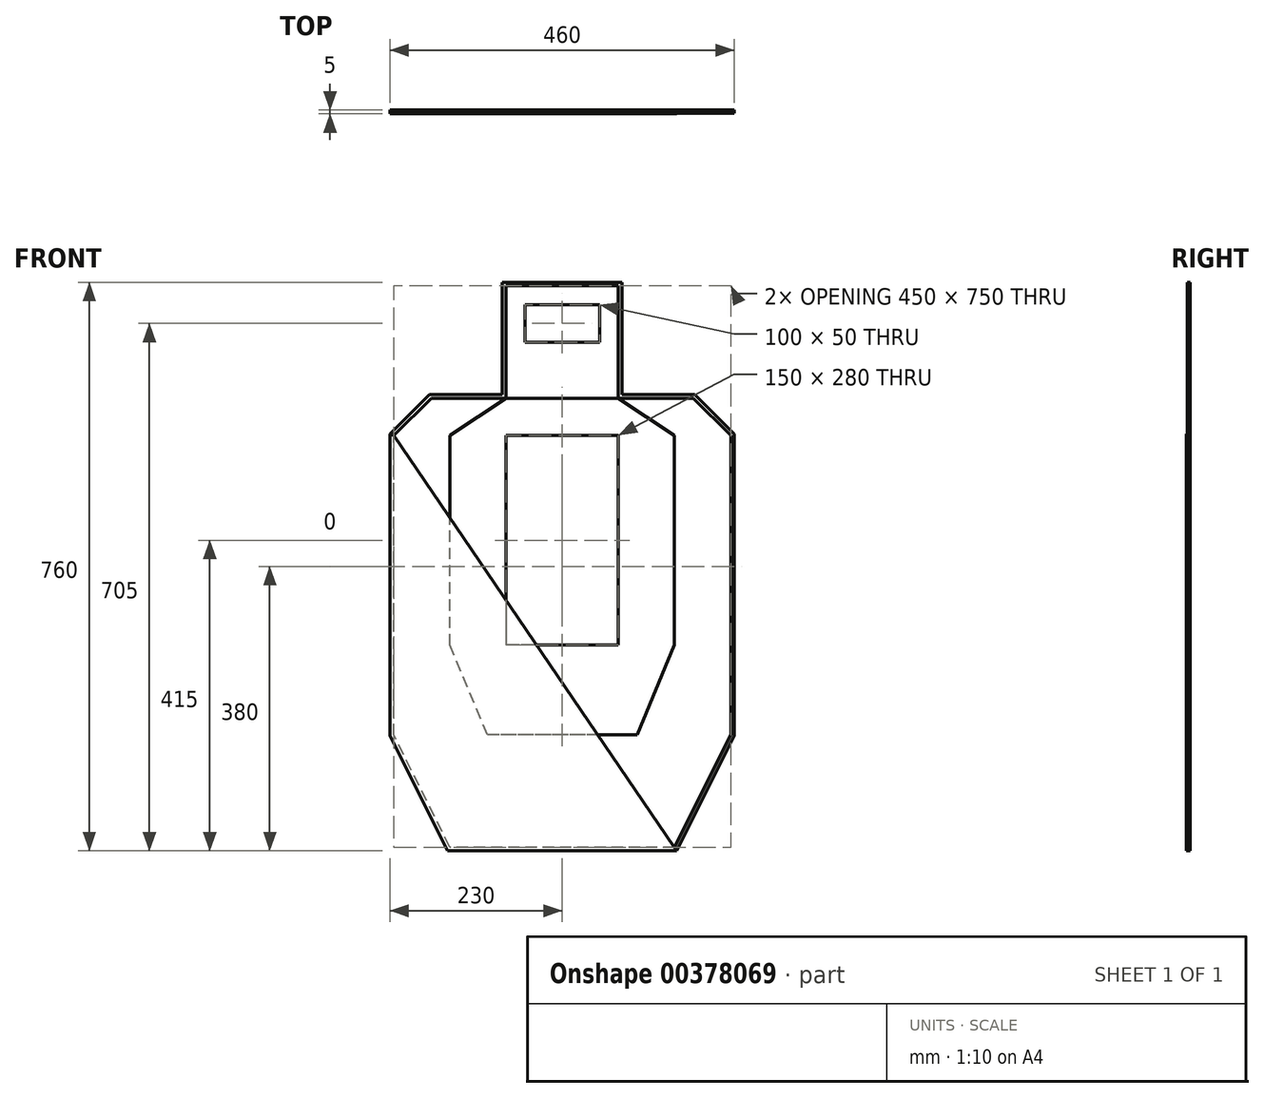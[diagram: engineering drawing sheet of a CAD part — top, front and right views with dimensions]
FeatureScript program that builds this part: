
annotation { "Feature Type Name" : "Feature", "Feature Type Description" : "" }
export const myFeature = defineFeature(function(context is Context, id is Id, definition is map)
    precondition{}
    {
        {
            var Q0;
            Q0=qCreatedBy(makeId("Front.planeOp"),FACE);
            var sketch = newSketch(context, id + "F0", { "sketchPlane" : qUnion([Q0])});
            skLineSegment(sketch, "E0.bottom", {"start": v(0, 100) * mm, "end": v(50, 100) * mm, "construction": true});
            skLineSegment(sketch, "E0.top", {"start": v(0, 125) * mm, "end": v(50, 125) * mm});
            skLineSegment(sketch, "E0.right", {"start": v(50, 100) * mm, "end": v(50, 125) * mm});
            skLineSegment(sketch, "E1.MirrorCS", {"start": v(0, 75) * mm, "end": v(50, 75) * mm});
            skLineSegment(sketch, "E2.MirrorCS", {"start": v(50, 100) * mm, "end": v(50, 75) * mm});
            skLineSegment(sketch, "E3.MirrorCS", {"start": v(0, 0) * mm, "end": v(0, 100) * mm, "construction": true});
            skLineSegment(sketch, "E4.MirrorCS", {"start": v(0, 125) * mm, "end": v(-50, 125) * mm});
            skLineSegment(sketch, "E5.MirrorCS", {"start": v(-50, 100) * mm, "end": v(-50, 125) * mm});
            skLineSegment(sketch, "E6.MirrorCS", {"start": v(-50, 100) * mm, "end": v(-50, 75) * mm});
            skLineSegment(sketch, "E7.MirrorCS", {"start": v(0, 75) * mm, "end": v(-50, 75) * mm});
            skSolve(sketch);
        }
        {
            var Q0;
            Q0=qSketchRegion(id+"F0",true);
            extrude(context, id + "F1", {"entities" : qUnion([Q0]), "oppositeDirection" : true, "depth" : 3 * mm});
        }
        {
            var Q0;
            Q0=qCreatedBy(makeId("Front.planeOp"),FACE);
            var sketch = newSketch(context, id + "F2", { "sketchPlane" : qUnion([Q0])});
            skLineSegment(sketch, "E8", {"start": v(75, 0) * mm, "end": v(75, 150) * mm});
            skLineSegment(sketch, "E9", {"start": v(75, 150) * mm, "end": v(-75, 150) * mm});
            skLineSegment(sketch, "E10", {"start": v(-75, 150) * mm, "end": v(-75, 0) * mm});
            skLineSegment(sketch, "E11", {"start": v(-75, 0) * mm, "end": v(75, 0) * mm});
            skLineSegment(sketch, "E12.0", {"start": v(0, 125) * mm, "end": v(-50, 125) * mm});
            skLineSegment(sketch, "E13.0", {"start": v(0, 125) * mm, "end": v(50, 125) * mm});
            skLineSegment(sketch, "E14.0", {"start": v(50, 100) * mm, "end": v(50, 125) * mm});
            skLineSegment(sketch, "E15.1", {"start": v(50, 100) * mm, "end": v(50, 75) * mm});
            skLineSegment(sketch, "E16.0", {"start": v(0, 75) * mm, "end": v(50, 75) * mm});
            skLineSegment(sketch, "E17.0", {"start": v(0, 75) * mm, "end": v(-50, 75) * mm});
            skLineSegment(sketch, "E18.0", {"start": v(-50, 100) * mm, "end": v(-50, 75) * mm});
            skLineSegment(sketch, "E19.1", {"start": v(-50, 100) * mm, "end": v(-50, 125) * mm});
            skLineSegment(sketch, "E20", {"start": v(0, 125) * mm, "end": v(0, 150) * mm, "construction": true});
            skLineSegment(sketch, "E21", {"start": v(0, 150) * mm, "end": v(0, 137.5) * mm, "construction": true});
            skSolve(sketch);
        }
        {
            var Q0;
            {var subQ0=sQuery(id+"F2.wireOp",EDGE,"E8");Q0=makeQuery(id+"F2.imprint","IMPRINT",FACE,{"disambiguationData":[TD([[makeQuery(id+"F2.imprint","IMPRINT",EDGE,{"derivedFrom":subQ0}),1.0]])]});}
            extrude(context, id + "F3", {"entities" : qUnion([Q0]), "oppositeDirection" : true, "depth" : 3 * mm});
        }
        {
            var Q0;
            Q0=qCreatedBy(makeId("Front.planeOp"),FACE);
            var sketch = newSketch(context, id + "F4", { "sketchPlane" : qUnion([Q0])});
            skLineSegment(sketch, "E22.bottom", {"start": v(75, -50) * mm, "end": v(-75, -50) * mm});
            skLineSegment(sketch, "E22.top", {"start": v(75, -330) * mm, "end": v(-75, -330) * mm});
            skLineSegment(sketch, "E22.left", {"start": v(75, -50) * mm, "end": v(75, -330) * mm});
            skLineSegment(sketch, "E22.right", {"start": v(-75, -50) * mm, "end": v(-75, -330) * mm});
            skLineSegment(sketch, "E23", {"start": v(0, 0) * mm, "end": v(0, -50) * mm, "construction": true});
            skLineSegment(sketch, "E24.0", {"start": v(-75, 0) * mm, "end": v(75, 0) * mm, "construction": true});
            skLineSegment(sketch, "E25", {"start": v(75, 0) * mm, "end": v(75, -50) * mm, "construction": true});
            skSolve(sketch);
        }
        {
            var Q0;
            Q0=makeQuery(id+"F4.imprint","IMPRINT",FACE,{"disambiguationData":[TD([[makeQuery(id+"F4.imprint","IMPRINT",EDGE,{"derivedFrom":sQuery(id+"F4.wireOp",EDGE,"E22.bottom")}),1.0]])]});
            extrude(context, id + "F5", {"entities" : qUnion([Q0]), "oppositeDirection" : true, "depth" : 3 * mm});
        }
        {
            var Q0;
            Q0=qCreatedBy(makeId("Front.planeOp"),FACE);
            var sketch = newSketch(context, id + "F6", { "sketchPlane" : qUnion([Q0])});
            skLineSegment(sketch, "E26.0", {"start": v(-75, 0) * mm, "end": v(75, 0) * mm});
            skLineSegment(sketch, "E27.1", {"start": v(75, -50) * mm, "end": v(75, -330) * mm});
            skLineSegment(sketch, "E28.2", {"start": v(75, -50) * mm, "end": v(-75, -50) * mm});
            skLineSegment(sketch, "E29.3", {"start": v(-75, -50) * mm, "end": v(-75, -330) * mm});
            skLineSegment(sketch, "E30.0", {"start": v(75, -330) * mm, "end": v(-75, -330) * mm});
            skLineSegment(sketch, "E31", {"start": v(75, 0) * mm, "end": v(150, -50) * mm});
            skLineSegment(sketch, "E32", {"start": v(150, -50) * mm, "end": v(150, -330) * mm});
            skLineSegment(sketch, "E33", {"start": v(150, -330) * mm, "end": v(100, -450) * mm});
            skLineSegment(sketch, "E34", {"start": v(100, -450) * mm, "end": v(-100, -450) * mm});
            skLineSegment(sketch, "E35", {"start": v(-100, -450) * mm, "end": v(-150, -330) * mm});
            skLineSegment(sketch, "E36", {"start": v(-150, -330) * mm, "end": v(-150, -50) * mm});
            skLineSegment(sketch, "E37", {"start": v(-150, -50) * mm, "end": v(-75, 0) * mm});
            skLineSegment(sketch, "E38", {"start": v(0, -450) * mm, "end": v(0, -50) * mm, "construction": true});
            skLineSegment(sketch, "E39", {"start": v(150, -50) * mm, "end": v(75, -50) * mm, "construction": true});
            skLineSegment(sketch, "E40", {"start": v(-55.04, -50) * mm, "end": v(-150, -50) * mm, "construction": true});
            skLineSegment(sketch, "E41", {"start": v(150, -330) * mm, "end": v(150, -450) * mm, "construction": true});
            skLineSegment(sketch, "E42", {"start": v(100, -450) * mm, "end": v(150, -450) * mm, "construction": true});
            skLineSegment(sketch, "E43", {"start": v(150, -330) * mm, "end": v(-150, -330) * mm, "construction": true});
            skLineSegment(sketch, "E44", {"start": v(-150, -330) * mm, "end": v(-150, -450) * mm, "construction": true});
            skLineSegment(sketch, "E45", {"start": v(-150, -450) * mm, "end": v(-100, -450) * mm, "construction": true});
            skSolve(sketch);
        }
        {
            var Q0;
            Q0=makeQuery(id+"F6.imprint","IMPRINT",FACE,{"disambiguationData":[TD([[makeQuery(id+"F6.imprint","IMPRINT",EDGE,{"derivedFrom":sQuery(id+"F6.wireOp",EDGE,"E26.0")}),-1.0]])]});
            extrude(context, id + "F7", {"entities" : qUnion([Q0]), "oppositeDirection" : true, "depth" : 3 * mm});
        }
        {
            var Q0;
            Q0=makeQuery(id+"F7.opExtrude","CAP_FACE",FACE,{"disambiguationData":[OSD([sQuery(id+"F6.wireOp",EDGE,"E26.0"),sQuery(id+"F6.wireOp",EDGE,"E27.1"),sQuery(id+"F6.wireOp",EDGE,"E28.2"),sQuery(id+"F6.wireOp",EDGE,"E29.3"),sQuery(id+"F6.wireOp",EDGE,"E30.0"),sQuery(id+"F6.wireOp",EDGE,"E31"),sQuery(id+"F6.wireOp",EDGE,"E32"),sQuery(id+"F6.wireOp",EDGE,"E33"),sQuery(id+"F6.wireOp",EDGE,"E34"),sQuery(id+"F6.wireOp",EDGE,"E35"),sQuery(id+"F6.wireOp",EDGE,"E36"),sQuery(id+"F6.wireOp",EDGE,"E37")])],"isStart":true});
            var sketch = newSketch(context, id + "F8", { "sketchPlane" : qUnion([Q0])});
            skLineSegment(sketch, "E46.0", {"start": v(75, 0) * mm, "end": v(150, -50) * mm});
            skLineSegment(sketch, "E47.0", {"start": v(150, -50) * mm, "end": v(150, -330) * mm});
            skLineSegment(sketch, "E48.0", {"start": v(150, -330) * mm, "end": v(100, -450) * mm});
            skLineSegment(sketch, "E49.1", {"start": v(100, -450) * mm, "end": v(-100, -450) * mm});
            skLineSegment(sketch, "E50.0", {"start": v(-150, -330) * mm, "end": v(-150, -50) * mm});
            skLineSegment(sketch, "E51.0", {"start": v(-100, -450) * mm, "end": v(-150, -330) * mm});
            skLineSegment(sketch, "E52.0", {"start": v(-150, -50) * mm, "end": v(-75, 0) * mm});
            skLineSegment(sketch, "E53", {"start": v(75, 0) * mm, "end": v(175, 0) * mm});
            skLineSegment(sketch, "E54", {"start": v(175, 0) * mm, "end": v(225, -50) * mm});
            skLineSegment(sketch, "E55", {"start": v(225, -50) * mm, "end": v(225, -450) * mm});
            skLineSegment(sketch, "E56", {"start": v(225, -450) * mm, "end": v(150, -600) * mm});
            skLineSegment(sketch, "E57", {"start": v(150, -600) * mm, "end": v(-150, -600) * mm});
            skLineSegment(sketch, "E58", {"start": v(-150, -600) * mm, "end": v(-225, -450) * mm});
            skLineSegment(sketch, "E59", {"start": v(-225, -450) * mm, "end": v(-225, -50) * mm});
            skLineSegment(sketch, "E60", {"start": v(-225, -50) * mm, "end": v(-175, 0) * mm});
            skLineSegment(sketch, "E61", {"start": v(-175, 0) * mm, "end": v(-75, 0) * mm});
            skLineSegment(sketch, "E62", {"start": v(225, -50) * mm, "end": v(225, 0) * mm, "construction": true});
            skLineSegment(sketch, "E63", {"start": v(225, 0) * mm, "end": v(175, 0) * mm, "construction": true});
            skLineSegment(sketch, "E64", {"start": v(225, -450) * mm, "end": v(225, -600) * mm, "construction": true});
            skLineSegment(sketch, "E65", {"start": v(225, -600) * mm, "end": v(150, -600) * mm, "construction": true});
            skLineSegment(sketch, "E66", {"start": v(-225, -450) * mm, "end": v(-225, -600) * mm, "construction": true});
            skLineSegment(sketch, "E67", {"start": v(-225, -600) * mm, "end": v(-150, -600) * mm, "construction": true});
            skLineSegment(sketch, "E68", {"start": v(-175, 0) * mm, "end": v(-225, 0) * mm, "construction": true});
            skLineSegment(sketch, "E69", {"start": v(-225, 0) * mm, "end": v(-225, -50) * mm, "construction": true});
            skSolve(sketch);
        }
        {
            var Q0;
            Q0=qSketchRegion(id+"F8",true);
            extrude(context, id + "F9", {"entities" : qUnion([Q0]), "oppositeDirection" : true, "depth" : 3 * mm});
        }
        {
            var Q0;
            Q0=makeQuery(id+"F9.opExtrude","CAP_FACE",FACE,{"disambiguationData":[OSD([sQuery(id+"F8.wireOp",EDGE,"E46.0"),sQuery(id+"F8.wireOp",EDGE,"E47.0"),sQuery(id+"F8.wireOp",EDGE,"E48.0"),sQuery(id+"F8.wireOp",EDGE,"E49.1"),sQuery(id+"F8.wireOp",EDGE,"E50.0"),sQuery(id+"F8.wireOp",EDGE,"E51.0"),sQuery(id+"F8.wireOp",EDGE,"E52.0"),sQuery(id+"F8.wireOp",EDGE,"E53"),sQuery(id+"F8.wireOp",EDGE,"E54"),sQuery(id+"F8.wireOp",EDGE,"E55"),sQuery(id+"F8.wireOp",EDGE,"E56"),sQuery(id+"F8.wireOp",EDGE,"E57"),sQuery(id+"F8.wireOp",EDGE,"E58"),sQuery(id+"F8.wireOp",EDGE,"E59"),sQuery(id+"F8.wireOp",EDGE,"E60"),sQuery(id+"F8.wireOp",EDGE,"E61")])],"isStart":true});
            var sketch = newSketch(context, id + "F10", { "sketchPlane" : qUnion([Q0])});
            skLineSegment(sketch, "E70.0", {"start": v(75, 150) * mm, "end": v(-75, 150) * mm});
            skLineSegment(sketch, "E71.0", {"start": v(75, 0) * mm, "end": v(75, 150) * mm});
            skLineSegment(sketch, "E72.1", {"start": v(75, 0) * mm, "end": v(175, 0) * mm});
            skLineSegment(sketch, "E73.0", {"start": v(175, 0) * mm, "end": v(225, -50) * mm});
            skLineSegment(sketch, "E74.1", {"start": v(225, -50) * mm, "end": v(225, -450) * mm});
            skLineSegment(sketch, "E75.0", {"start": v(225, -450) * mm, "end": v(150, -600) * mm});
            skLineSegment(sketch, "E76.1", {"start": v(150, -600) * mm, "end": v(-150, -600) * mm});
            skLineSegment(sketch, "E77.2", {"start": v(-150, -600) * mm, "end": v(-225, -450) * mm});
            skLineSegment(sketch, "E78.3", {"start": v(-225, -450) * mm, "end": v(-225, -50) * mm});
            skLineSegment(sketch, "E79.4", {"start": v(-225, -50) * mm, "end": v(-175, 0) * mm});
            skLineSegment(sketch, "E80.5", {"start": v(-175, 0) * mm, "end": v(-75, 0) * mm});
            skLineSegment(sketch, "E81.0", {"start": v(-75, 150) * mm, "end": v(-75, 0) * mm});
            skLineSegment(sketch, "E82.0", {"start": v(177.07, 5) * mm, "end": v(230, -47.93) * mm});
            skLineSegment(sketch, "E82.1", {"start": v(-230, -451.18) * mm, "end": v(-230, -47.93) * mm});
            skLineSegment(sketch, "E82.2", {"start": v(-153.1, -605) * mm, "end": v(-230, -451.18) * mm});
            skLineSegment(sketch, "E82.3", {"start": v(153.1, -605) * mm, "end": v(-153.1, -605) * mm});
            skLineSegment(sketch, "E82.4", {"start": v(230, -451.18) * mm, "end": v(153.1, -605) * mm});
            skLineSegment(sketch, "E82.5", {"start": v(-230, -47.93) * mm, "end": v(-177.07, 5) * mm});
            skLineSegment(sketch, "E82.6", {"start": v(230, -47.93) * mm, "end": v(230, -451.18) * mm});
            skLineSegment(sketch, "E82.7", {"start": v(-177.07, 5) * mm, "end": v(-80, 5) * mm});
            skLineSegment(sketch, "E82.8", {"start": v(-80, 155) * mm, "end": v(-80, 5) * mm});
            skLineSegment(sketch, "E82.9", {"start": v(80, 155) * mm, "end": v(-80, 155) * mm});
            skLineSegment(sketch, "E82.10", {"start": v(80, 5) * mm, "end": v(80, 155) * mm});
            skLineSegment(sketch, "E82.11", {"start": v(80, 5) * mm, "end": v(177.07, 5) * mm});
            skSolve(sketch);
        }
        {
            var Q0;
            Q0=makeQuery(id+"F10.imprint","IMPRINT",FACE,{"disambiguationData":[TD([[makeQuery(id+"F10.imprint","IMPRINT",EDGE,{"derivedFrom":sQuery(id+"F10.wireOp",EDGE,"E70.0")}),-1.0]])]});
            extrude(context, id + "F11", {"entities" : qUnion([Q0]), "oppositeDirection" : true, "depth" : 3 * mm});
        }
        {
            var Q0;
            Q0=makeQuery(id+"F9.opExtrude","CAP_FACE",FACE,{"disambiguationData":[OSD([sQuery(id+"F8.wireOp",EDGE,"E46.0"),sQuery(id+"F8.wireOp",EDGE,"E47.0"),sQuery(id+"F8.wireOp",EDGE,"E48.0"),sQuery(id+"F8.wireOp",EDGE,"E49.1"),sQuery(id+"F8.wireOp",EDGE,"E50.0"),sQuery(id+"F8.wireOp",EDGE,"E51.0"),sQuery(id+"F8.wireOp",EDGE,"E52.0"),sQuery(id+"F8.wireOp",EDGE,"E53"),sQuery(id+"F8.wireOp",EDGE,"E54"),sQuery(id+"F8.wireOp",EDGE,"E55"),sQuery(id+"F8.wireOp",EDGE,"E56"),sQuery(id+"F8.wireOp",EDGE,"E57"),sQuery(id+"F8.wireOp",EDGE,"E58"),sQuery(id+"F8.wireOp",EDGE,"E59"),sQuery(id+"F8.wireOp",EDGE,"E60"),sQuery(id+"F8.wireOp",EDGE,"E61")])],"isStart":false});
            var sketch = newSketch(context, id + "F12", { "sketchPlane" : qUnion([Q0])});
            skLineSegment(sketch, "E83.0", {"start": v(75, 150) * mm, "end": v(75, 0) * mm});
            skLineSegment(sketch, "E84.0", {"start": v(175, 0) * mm, "end": v(75, 0) * mm});
            skLineSegment(sketch, "E85.0", {"start": v(-75, 150) * mm, "end": v(75, 150) * mm});
            skLineSegment(sketch, "E86.0", {"start": v(225, -50) * mm, "end": v(175, 0) * mm});
            skLineSegment(sketch, "E87.0", {"start": v(-225, -50) * mm, "end": v(-225, -450) * mm});
            skLineSegment(sketch, "E87.1", {"start": v(225, -450) * mm, "end": v(225, -50) * mm});
            skLineSegment(sketch, "E87.2", {"start": v(150, -600) * mm, "end": v(225, -450) * mm});
            skLineSegment(sketch, "E87.3", {"start": v(-225, -450) * mm, "end": v(-150, -600) * mm});
            skLineSegment(sketch, "E87.4", {"start": v(-150, -600) * mm, "end": v(150, -600) * mm});
            skLineSegment(sketch, "E88.0", {"start": v(-175, 0) * mm, "end": v(-225, -50) * mm});
            skLineSegment(sketch, "E89.0", {"start": v(-75, 0) * mm, "end": v(-175, 0) * mm});
            skLineSegment(sketch, "E90.0", {"start": v(-75, 0) * mm, "end": v(-75, 150) * mm});
            skSolve(sketch);
        }
        {
            var Q0;
            Q0=qSketchRegion(id+"F12",true);
            extrude(context, id + "F13", {"entities" : qUnion([Q0]), "depth" : 1 * mm});
        }
        {
            var Q0;
            Q0=makeQuery(id+"F13.opExtrude","CAP_FACE",FACE,{"disambiguationData":[OSD([sQuery(id+"F12.wireOp",EDGE,"E83.0"),sQuery(id+"F12.wireOp",EDGE,"E84.0"),sQuery(id+"F12.wireOp",EDGE,"E85.0"),sQuery(id+"F12.wireOp",EDGE,"E86.0"),sQuery(id+"F12.wireOp",EDGE,"E87.0"),sQuery(id+"F12.wireOp",EDGE,"E87.1"),sQuery(id+"F12.wireOp",EDGE,"E87.2"),sQuery(id+"F12.wireOp",EDGE,"E87.3"),sQuery(id+"F12.wireOp",EDGE,"E87.4"),sQuery(id+"F12.wireOp",EDGE,"E88.0"),sQuery(id+"F12.wireOp",EDGE,"E89.0"),sQuery(id+"F12.wireOp",EDGE,"E90.0")])],"isStart":false});
            var sketch = newSketch(context, id + "F14", { "sketchPlane" : qUnion([Q0])});
            skLineSegment(sketch, "E91.0", {"start": v(-80, 155) * mm, "end": v(80, 155) * mm});
            skLineSegment(sketch, "E92.0", {"start": v(80, 155) * mm, "end": v(80, 5) * mm});
            skLineSegment(sketch, "E93.0", {"start": v(-80, 5) * mm, "end": v(-80, 155) * mm});
            skLineSegment(sketch, "E94.0", {"start": v(177.07, 5) * mm, "end": v(80, 5) * mm});
            skLineSegment(sketch, "E95.0", {"start": v(-80, 5) * mm, "end": v(-177.07, 5) * mm});
            skLineSegment(sketch, "E96.0", {"start": v(230, -47.93) * mm, "end": v(177.07, 5) * mm});
            skLineSegment(sketch, "E97.0", {"start": v(-177.07, 5) * mm, "end": v(-230, -47.93) * mm});
            skLineSegment(sketch, "E98.1", {"start": v(-230, -47.93) * mm, "end": v(-230, -451.18) * mm});
            skLineSegment(sketch, "E99.0", {"start": v(-230, -451.18) * mm, "end": v(-153.1, -605) * mm});
            skLineSegment(sketch, "E100.0", {"start": v(-153.1, -605) * mm, "end": v(153.1, -605) * mm});
            skLineSegment(sketch, "E101.0", {"start": v(153.1, -605) * mm, "end": v(230, -451.18) * mm});
            skLineSegment(sketch, "E102.0", {"start": v(230, -451.18) * mm, "end": v(230, -47.93) * mm});
            skLineSegment(sketch, "E103.0", {"start": v(-75, 150) * mm, "end": v(75, 150) * mm});
            skLineSegment(sketch, "E104.0", {"start": v(-75, 0) * mm, "end": v(-75, 150) * mm});
            skLineSegment(sketch, "E105.0", {"start": v(75, 150) * mm, "end": v(75, 0) * mm});
            skLineSegment(sketch, "E106.0", {"start": v(175, 0) * mm, "end": v(75, 0) * mm});
            skLineSegment(sketch, "E107.0", {"start": v(225, -50) * mm, "end": v(175, 0) * mm});
            skLineSegment(sketch, "E108.0", {"start": v(150, -600) * mm, "end": v(225, -450) * mm});
            skLineSegment(sketch, "E109.0", {"start": v(225, -450) * mm, "end": v(225, -50) * mm});
            skLineSegment(sketch, "E110.0", {"start": v(-150, -600) * mm, "end": v(150, -600) * mm});
            skLineSegment(sketch, "E111.0", {"start": v(-225, -450) * mm, "end": v(-150, -600) * mm});
            skLineSegment(sketch, "E112.0", {"start": v(-225, -50) * mm, "end": v(-225, -450) * mm});
            skLineSegment(sketch, "E113.0", {"start": v(-175, 0) * mm, "end": v(-225, -50) * mm});
            skLineSegment(sketch, "E114.0", {"start": v(-75, 0) * mm, "end": v(-175, 0) * mm});
            skSolve(sketch);
        }
        {
            var Q0;
            Q0=makeQuery(id+"F14.imprint","IMPRINT",FACE,{"disambiguationData":[TD([[makeQuery(id+"F14.imprint","IMPRINT",EDGE,{"derivedFrom":sQuery(id+"F14.wireOp",EDGE,"E91.0")}),-1.0]])]});
            extrude(context, id + "F15", {"entities" : qUnion([Q0]), "oppositeDirection" : true, "depth" : 1 * mm});
        }
        {
            var Q0;
            Q0=makeQuery(id+"F9.opExtrude","CAP_FACE",FACE,{"disambiguationData":[OSD([sQuery(id+"F8.wireOp",EDGE,"E46.0"),sQuery(id+"F8.wireOp",EDGE,"E47.0"),sQuery(id+"F8.wireOp",EDGE,"E48.0"),sQuery(id+"F8.wireOp",EDGE,"E49.1"),sQuery(id+"F8.wireOp",EDGE,"E50.0"),sQuery(id+"F8.wireOp",EDGE,"E51.0"),sQuery(id+"F8.wireOp",EDGE,"E52.0"),sQuery(id+"F8.wireOp",EDGE,"E53"),sQuery(id+"F8.wireOp",EDGE,"E54"),sQuery(id+"F8.wireOp",EDGE,"E55"),sQuery(id+"F8.wireOp",EDGE,"E56"),sQuery(id+"F8.wireOp",EDGE,"E57"),sQuery(id+"F8.wireOp",EDGE,"E58"),sQuery(id+"F8.wireOp",EDGE,"E59"),sQuery(id+"F8.wireOp",EDGE,"E60"),sQuery(id+"F8.wireOp",EDGE,"E61")])],"isStart":true});
            var sketch = newSketch(context, id + "F16", { "sketchPlane" : qUnion([Q0])});
            skLineSegment(sketch, "E115.0", {"start": v(-153.1, -605) * mm, "end": v(-230, -451.18) * mm});
            skLineSegment(sketch, "E116.0", {"start": v(-230, -451.18) * mm, "end": v(-230, -47.93) * mm});
            skLineSegment(sketch, "E117.0", {"start": v(153.1, -605) * mm, "end": v(-153.1, -605) * mm});
            skLineSegment(sketch, "E118", {"start": v(-230, -47.93) * mm, "end": v(-225, -50) * mm});
            skLineSegment(sketch, "E119", {"start": v(-225, -50) * mm, "end": v(150, -600) * mm});
            skLineSegment(sketch, "E120", {"start": v(150, -600) * mm, "end": v(153.1, -605) * mm});
            skSolve(sketch);
        }
        {
            var Q0;
            Q0=qSketchRegion(id+"F16",true);
            extrude(context, id + "F17", {"entities" : qUnion([Q0]), "depth" : 1 * mm});
        }
    });
